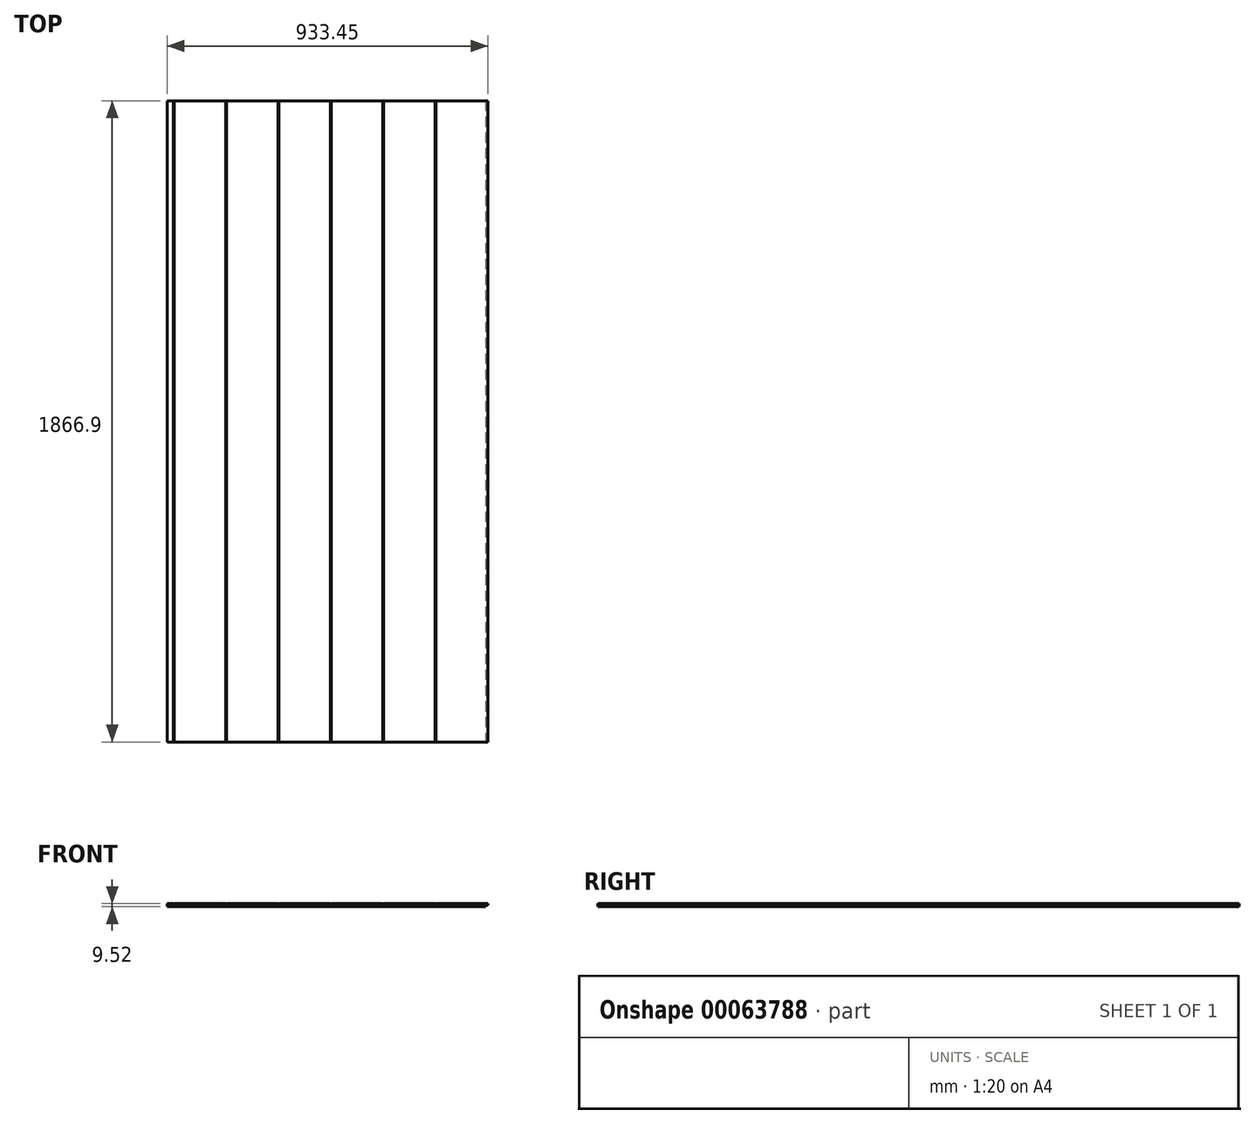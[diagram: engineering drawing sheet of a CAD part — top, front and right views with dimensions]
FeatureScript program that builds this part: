
annotation { "Feature Type Name" : "Feature", "Feature Type Description" : "" }
export const myFeature = defineFeature(function(context is Context, id is Id, definition is map)
    precondition{}
    {
        {
            var Q0;
            Q0=qCreatedBy(makeId("Top.planeOp"),FACE);
            var sketch = newSketch(context, id + "F0", { "sketchPlane" : qUnion([Q0])});
            skLineSegment(sketch, "E0.bottom", {"start": v(-609.6, 1911.45) * mm, "end": v(609.6, 1911.45) * mm});
            skLineSegment(sketch, "E0.top", {"start": v(-609.6, -523.78) * mm, "end": v(609.6, -523.78) * mm});
            skLineSegment(sketch, "E0.left", {"start": v(-609.6, 1911.45) * mm, "end": v(-609.6, -523.78) * mm});
            skLineSegment(sketch, "E0.right", {"start": v(609.6, 1911.45) * mm, "end": v(609.6, -523.78) * mm});
            skSolve(sketch);
        }
        {
            var Q0;
            Q0=qSketchRegion(id+"F0",true);
            extrude(context, id + "F1", {"entities" : qUnion([Q0]), "endBound" : BoundingType.SYMMETRIC, "depth" : 9.52 * mm});
        }
        {
            var Q0;
            Q0=makeQuery(id+"F1.opExtrude","SWEPT_FACE",FACE,{"disambiguationData":[OSD([sQuery(id+"F0.wireOp",EDGE,"E0.top")])]});
            var sketch = newSketch(context, id + "F2", { "sketchPlane" : qUnion([Q0])});
            skLineSegment(sketch, "E1", {"start": v(609.6, 0) * mm, "end": v(603.25, 0) * mm});
            skPoint(sketch, "E1.endSnap0", {"position": v(609.6, 0) * mm});
            skLineSegment(sketch, "E2", {"start": v(603.25, 0) * mm, "end": v(603.25, -4.76) * mm});
            skLineSegment(sketch, "E3", {"start": v(609.6, 0) * mm, "end": v(609.6, -4.76) * mm});
            skLineSegment(sketch, "E4", {"start": v(609.6, -4.76) * mm, "end": v(603.25, -4.76) * mm});
            skLineSegment(sketch, "E5.bottom", {"start": v(-609.6, 4.76) * mm, "end": v(-603.25, 4.76) * mm});
            skLineSegment(sketch, "E5.top", {"start": v(-609.6, 0) * mm, "end": v(-603.25, 0) * mm});
            skLineSegment(sketch, "E5.left", {"start": v(-609.6, 4.76) * mm, "end": v(-609.6, 0) * mm});
            skLineSegment(sketch, "E5.right", {"start": v(-603.25, 4.76) * mm, "end": v(-603.25, 0) * mm});
            skSolve(sketch);
        }
        {
            var Q0;
            Q0=qSketchRegion(id+"F2",true);
            extrude(context, id + "F3", {"entities" : qUnion([Q0]), "operationType" : NewBodyOperationType.REMOVE, "endBound" : BoundingType.THROUGH_ALL, "oppositeDirection" : true, "depth" : 25.4 * mm});
        }
        {
            var Q0;
            Q0=makeQuery(id+"F1.opExtrude","SWEPT_FACE",FACE,{"disambiguationData":[OSD([sQuery(id+"F0.wireOp",EDGE,"E0.top")])]});
            var sketch = newSketch(context, id + "F4", { "sketchPlane" : qUnion([Q0])});
            skLineSegment(sketch, "E6.bottom", {"start": v(-458, 4.76) * mm, "end": v(-456.4, 4.76) * mm});
            skLineSegment(sketch, "E6.top", {"start": v(-458, 3.17) * mm, "end": v(-456.4, 3.17) * mm});
            skLineSegment(sketch, "E6.left", {"start": v(-458, 4.76) * mm, "end": v(-458, 3.17) * mm});
            skLineSegment(sketch, "E6.right", {"start": v(-456.4, 4.76) * mm, "end": v(-456.4, 3.17) * mm});
            skPoint(sketch, "E7", {"position": v(-457.2, 3.17) * mm});
            skPoint(sketch, "E8.1.0.0", {"position": v(-304.8, 3.17) * mm});
            skLineSegment(sketch, "E8.1.0.1", {"start": v(-305.6, 4.76) * mm, "end": v(-304, 4.76) * mm});
            skLineSegment(sketch, "E8.1.0.2", {"start": v(-305.6, 3.17) * mm, "end": v(-304, 3.17) * mm});
            skLineSegment(sketch, "E8.1.0.3", {"start": v(-305.6, 4.76) * mm, "end": v(-305.6, 3.17) * mm});
            skLineSegment(sketch, "E8.1.0.4", {"start": v(-304, 4.76) * mm, "end": v(-304, 3.17) * mm});
            skPoint(sketch, "E8.2.0.0", {"position": v(-152.4, 3.17) * mm});
            skLineSegment(sketch, "E8.2.0.1", {"start": v(-153.2, 4.76) * mm, "end": v(-151.6, 4.76) * mm});
            skLineSegment(sketch, "E8.2.0.2", {"start": v(-153.2, 3.17) * mm, "end": v(-151.6, 3.17) * mm});
            skLineSegment(sketch, "E8.2.0.3", {"start": v(-153.2, 4.76) * mm, "end": v(-153.2, 3.17) * mm});
            skLineSegment(sketch, "E8.2.0.4", {"start": v(-151.6, 4.76) * mm, "end": v(-151.6, 3.17) * mm});
            skPoint(sketch, "E8.3.0.0", {"position": v(0, 3.17) * mm});
            skLineSegment(sketch, "E8.3.0.1", {"start": v(-0.8, 4.76) * mm, "end": v(0.8, 4.76) * mm});
            skLineSegment(sketch, "E8.3.0.2", {"start": v(-0.8, 3.17) * mm, "end": v(0.8, 3.17) * mm});
            skLineSegment(sketch, "E8.3.0.3", {"start": v(-0.8, 4.76) * mm, "end": v(-0.8, 3.17) * mm});
            skLineSegment(sketch, "E8.3.0.4", {"start": v(0.8, 4.76) * mm, "end": v(0.8, 3.17) * mm});
            skPoint(sketch, "E8.4.0.0", {"position": v(152.4, 3.17) * mm});
            skLineSegment(sketch, "E8.4.0.1", {"start": v(151.6, 4.76) * mm, "end": v(153.2, 4.76) * mm});
            skLineSegment(sketch, "E8.4.0.2", {"start": v(151.6, 3.17) * mm, "end": v(153.2, 3.17) * mm});
            skLineSegment(sketch, "E8.4.0.3", {"start": v(151.6, 4.76) * mm, "end": v(151.6, 3.17) * mm});
            skLineSegment(sketch, "E8.4.0.4", {"start": v(153.2, 4.76) * mm, "end": v(153.2, 3.17) * mm});
            skPoint(sketch, "E8.5.0.0", {"position": v(304.8, 3.17) * mm});
            skLineSegment(sketch, "E8.5.0.1", {"start": v(304, 4.76) * mm, "end": v(305.6, 4.76) * mm});
            skLineSegment(sketch, "E8.5.0.2", {"start": v(304, 3.17) * mm, "end": v(305.6, 3.17) * mm});
            skLineSegment(sketch, "E8.5.0.3", {"start": v(304, 4.76) * mm, "end": v(304, 3.17) * mm});
            skLineSegment(sketch, "E8.5.0.4", {"start": v(305.6, 4.76) * mm, "end": v(305.6, 3.17) * mm});
            skPoint(sketch, "E8.6.0.0", {"position": v(457.2, 3.17) * mm});
            skLineSegment(sketch, "E8.6.0.1", {"start": v(456.4, 4.76) * mm, "end": v(458, 4.76) * mm});
            skLineSegment(sketch, "E8.6.0.2", {"start": v(456.4, 3.17) * mm, "end": v(458, 3.17) * mm});
            skLineSegment(sketch, "E8.6.0.3", {"start": v(456.4, 4.76) * mm, "end": v(456.4, 3.17) * mm});
            skLineSegment(sketch, "E8.6.0.4", {"start": v(458, 4.76) * mm, "end": v(458, 3.17) * mm});
            skLineSegment(sketch, "E8.direction1", {"start": v(-457.2, 3.17) * mm, "end": v(-304.8, 3.17) * mm, "construction": true});
            skSolve(sketch);
        }
        {
            var Q0;
            Q0=qSketchRegion(id+"F4",true);
            extrude(context, id + "F5", {"entities" : qUnion([Q0]), "operationType" : NewBodyOperationType.REMOVE, "endBound" : BoundingType.THROUGH_ALL, "oppositeDirection" : true, "depth" : 25.4 * mm});
        }
        {
            var Q0;
            Q0=makeQuery(id+"F1.opExtrude","SWEPT_FACE",FACE,{"disambiguationData":[OSD([sQuery(id+"F0.wireOp",EDGE,"E0.top")])]});
            var sketch = newSketch(context, id + "F6", { "sketchPlane" : qUnion([Q0])});
            skLineSegment(sketch, "E9", {"start": v(-0.8, 3.17) * mm, "end": v(0, 3.17) * mm});
            skLineSegment(sketch, "E10.bottom", {"start": v(-609.6, -4.76) * mm, "end": v(-323.85, -4.76) * mm});
            skLineSegment(sketch, "E10.top", {"start": v(-609.6, 4.76) * mm, "end": v(-323.85, 4.76) * mm});
            skLineSegment(sketch, "E10.left", {"start": v(-609.6, -4.76) * mm, "end": v(-609.6, 4.76) * mm});
            skLineSegment(sketch, "E10.right", {"start": v(-323.85, -4.76) * mm, "end": v(-323.85, 4.76) * mm});
            skSolve(sketch);
        }
        {
            var Q0;
            Q0 = qSketchRegion(id + "F6", true);
            extrude(context, id + "F7", {"entities" : qUnion([Q0]), "operationType" : NewBodyOperationType.REMOVE, "endBound" : BoundingType.THROUGH_ALL, "oppositeDirection" : true, "depth" : 25.4 * mm});
        }
        {
            var Q0;
            Q0=makeQuery(id+"F7.boolean.opBoolean","COPY",FACE,{"derivedFrom":makeQuery(id+"F7.opExtrude","SWEPT_FACE",FACE,{"disambiguationData":[OSD([sQuery(id+"F6.wireOp",EDGE,"E10.right")])]})});
            var sketch = newSketch(context, id + "F8", { "sketchPlane" : qUnion([Q0])});
            skLineSegment(sketch, "E11.bottom", {"start": v(-1911.45, -4.76) * mm, "end": v(-1343.12, -4.76) * mm});
            skLineSegment(sketch, "E11.top", {"start": v(-1911.45, 4.76) * mm, "end": v(-1343.12, 4.76) * mm});
            skLineSegment(sketch, "E11.left", {"start": v(-1911.45, -4.76) * mm, "end": v(-1911.45, 4.76) * mm});
            skLineSegment(sketch, "E11.right", {"start": v(-1343.12, -4.76) * mm, "end": v(-1343.12, 4.76) * mm});
            skSolve(sketch);
        }
        {
            var Q0;
            Q0 = qSketchRegion(id + "F8", true);
            extrude(context, id + "F9", {"entities" : qUnion([Q0]), "operationType" : NewBodyOperationType.REMOVE, "endBound" : BoundingType.THROUGH_ALL, "oppositeDirection" : true, "depth" : 25.4 * mm});
        }
    });
